# Revit family: Konsole 35- 35 Platte längs
name_source: partatom
category: HLS-Bauteile
revit_build: Autodesk Revit 2017 (Build: 20190507_1515(x64)
units: mm (PartAtom-declared; Revit-internal decimal feet)

## family parameters
Basisbauteil = Fläche
Beim Laden mit Abzugskörper schneiden = Nein
Bemaßung runder Anschluss = Durchmesser verwenden
Gemeinsam genutzt = Ja
Raumberechnungspunkt = Nein
Teiletyp = Normal

## types (6) — shared parameters
Ausrichtung Platte = längs
Breite Platte = 45 mm  [stored 0.147638 ft]
Breite Profil = 35 mm  [stored 0.114829 ft]
Fabrikat = MEFA
Firma = MEFA Befestigungs- und Montagesysteme GmbH
Höhe Profil = 35 mm  [stored 0.114829 ft]
Kurztext1 = Konsole Stex 35/35
Langloch Platte = 11x15 mm
Lochabstand = 75 mm
Lochdurchmesser = 11 mm
Länge Platte = 100 mm  [stored 0.328084 ft]
Material = Stahl
Materialname C-Profil = S235JR
Materialname Platte = S235JR
Oberflaeche = galvanisch verzinkt
Profil = Stex
Stärke Platte = 4 mm  [stored 0.0131234 ft]
Stärke Profil = 1 mm  [stored 0.00328084 ft]
Vorgabe-Ansicht = 1219 mm

## per-type parameters (varying)
| type | Artikelnummer | EAN | Gewicht | Gewicht pro Bauteil | Kurztext2 | Länge Konsole | Schienenlänge | max. zul. Last F1 | max. zul. Last F2 | max. zul. Last q0 |
| Konsole 35- 35 L=  525 Platte längs gvz | 1274525 | 4250928424525 | 0.67 kg | 0.67 kg | L= 525 mm Platte längs gvz | 525 mm | Montageschiene 35- 35-1,0 für Konsole : C-Profil 35- 35-1,0 L=  525 | 0.13 kip | 0.06 kip | 0.076 kip/ft |
| Konsole 35- 35 L=  450 Platte längs gvz | 1274450 | 4250928424518 | 0.59 kg | 0.59 kg | L= 450 mm Platte längs gvz | 450 mm  [stored 1.47638 ft] | Montageschiene 35- 35-1,0 für Konsole : C-Profil 35- 35-1,0 L=  450 | 0.15 kip | 0.08 kip | 0.104 kip/ft |
| Konsole 35- 35 L=  375 Platte längs gvz | 1274375 | 4250928424501 | 0.52 kg | 0.52 kg | L= 375 mm Platte längs gvz | 375 mm  [stored 1.23031 ft] | Montageschiene 35- 35-1,0 für Konsole : C-Profil 35- 35-1,0 L=  375 | 0.18 kip | 0.09 kip | 0.149 kip/ft |
| Konsole 35- 35 L=  300 Platte längs gvz | 1274300 | 4250928424495 | 0.44 kg | 0.44 kg | L= 300 mm Platte längs gvz | 300 mm | Montageschiene 35- 35-1,0 für Konsole : C-Profil 35- 35-1,0 L=  300 | 0.23 kip | 0.11 kip | 0.234 kip/ft |
| Konsole 35- 35 L=  225 Platte längs gvz | 1274225 | 4250928424488 | 0.36 kg | 0.36 kg | L= 225 mm Platte längs gvz | 225 mm  [stored 0.738189 ft] | Montageschiene 35- 35-1,0 für Konsole : C-Profil 35- 35-1,0 L=  225 | 0.31 kip | 0.15 kip | 0.416 kip/ft |
| Konsole 35- 35 L=  150 Platte längs gvz | 1274150 | 4250928424471 | 0.29 kg | 0.29 kg | L= 150 mm Platte längs gvz | 150 mm  [stored 0.492126 ft] | Montageschiene 35- 35-1,0 für Konsole : C-Profil 35- 35-1,0 L=  150 | 0.46 kip | 0.23 kip | 0.935 kip/ft |

note: [stored X ft] marks values corroborated as IEEE doubles in the binary element streams (Revit-internal decimal feet)
